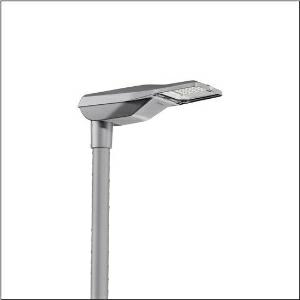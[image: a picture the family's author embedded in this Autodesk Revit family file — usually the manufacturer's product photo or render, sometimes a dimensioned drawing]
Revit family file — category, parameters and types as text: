
# Revit family: streetlight_sl_21_iq_micro___p0_5a_5xe1v31g08cb_6456
name_source: partatom
category: Lighting Fixtures
units: mm (PartAtom-declared; Revit-internal decimal feet)

## family parameters
Cut with Voids When Loaded = No
Host = Face
Light Source = No
Part Type = Normal
Room Calculation Point = No
Round Connector Dimension = Use Diameter
Shared = No

## types (1)
- --- (1 x LED, 2780 lm, 19.4 W, 3000K)
    Apparent Load = 19 VA
    CIE Flux Codes = 37 73 96 100 100
    Color Rendering = 70
    Color Temperature = 3000K
    Default Elevation = 1800 mm
    Description = Streetlight SL 21 iQ micro, mast luminaire, primary light control with lens, of PMMA, primary optical cover: cover, of toughened safety glass, transparent, light distribution: P0.5a, light emission: direct distribution, primary light characteristic: asymmetric, installation type: post-top, side-entry, LED, High Power LED, rated luminous flux: 2.780lm, luminous efficacy: 143lm/W, light colour: 730, colour temperature: 3000K, control gear: iQ Street-Remote, control: pre-setting: linear dimming characteristic, Street-Remote, Auto-Match, Temp-Guard, Lumen-Switch, Night-Set, Smart-Wire, Light-Fading, Desk-Remote (wireless, voltage-free reading and setting of iQ features in the workshop via application-optimized NFC function/RFID function), optimised constant luminous flux control (CLO 2.0), mains connection: 220..240V, AC, 50/60Hz, start of lifetime: 19W, end of service life: 20W, reduction: 10W, luminaire housing, of diecast aluminium, powder-coated, SITECO metallic grey (DB 702S), corrosivity category C5 high according to DIN EN ISO 12944, please order mast flange separately, inclination adjustable: 0°, 5°, 10°, 15°, sealing non-destructively replaceable, multi-level sealing system, length: 528mm, width: 235mm, height: 110mm, mast flange for spigot size: 42mm (side-entry): 5XC10008XM4, 60/48mm (side-entry/post-top): 5XC10108XM2, 76/60mm (side-entry/post-top): 5XC10108XM1, protection rating (complete): IP66, insulation class (complete): insulation class II (safety insulation), certification: CE, ENEC, ENEC+, VDE, impact resistance: IK10, permissible operating ambient temperature for outdoor applications: -40..+50°C, standard-compliant lighting for roads and squares, packaging unit: 1 piece

Light Distribution: P0.5a
    Height = 110 mm
    Lamp = 1 x LED
    Lamp Light Flux = 2780 lm
    Lamp Power = 19.4 W
    Lamp count = 1
    Length = 528 mm
    Luminous efficacy = 143 lm/W
    Manufacturer = Siteco
    ModVariant = No
    Model = 5XE1V31G08CB
    Number of Poles = 1
    OnlyDefault = Yes
    Power Factor = 1
    Product Name = Streetlight SL 21 iQ micro | P0.5a
    Product group = mast luminaire | pylon top
    ProductGroupID = 6100
    Protection Class = Protection class II
    Protection Degree = IP 66
    RLX_Detail_Level = 1
    RLX_Emergency_Light_Flux = 0 lm
    RLX_Emergency_Type = 0
    RLX_Emergency_Type_DB = No
    RlxData = <blob elided: 98209 chars, md5=3c7c8078>
    Socket = socket
    Standby Power = 0 W
    System Light Flux = 2780 lm
    System Power = 19 W
    Type Comments = factory setting: luminous flux: 100 % | dim-lin: 254 | 387 mA
    Type Image = l_1006881.jpg
    URL = http://relux.com
    VarID = @adj_078035
    Voltage = 0 V
    Weight = 0.00 kg
    Width = 235 mm

## geometry (parser evidence)
native form markers: Blend x4, Sweep x9
no freeform markers — native parametric forms only
